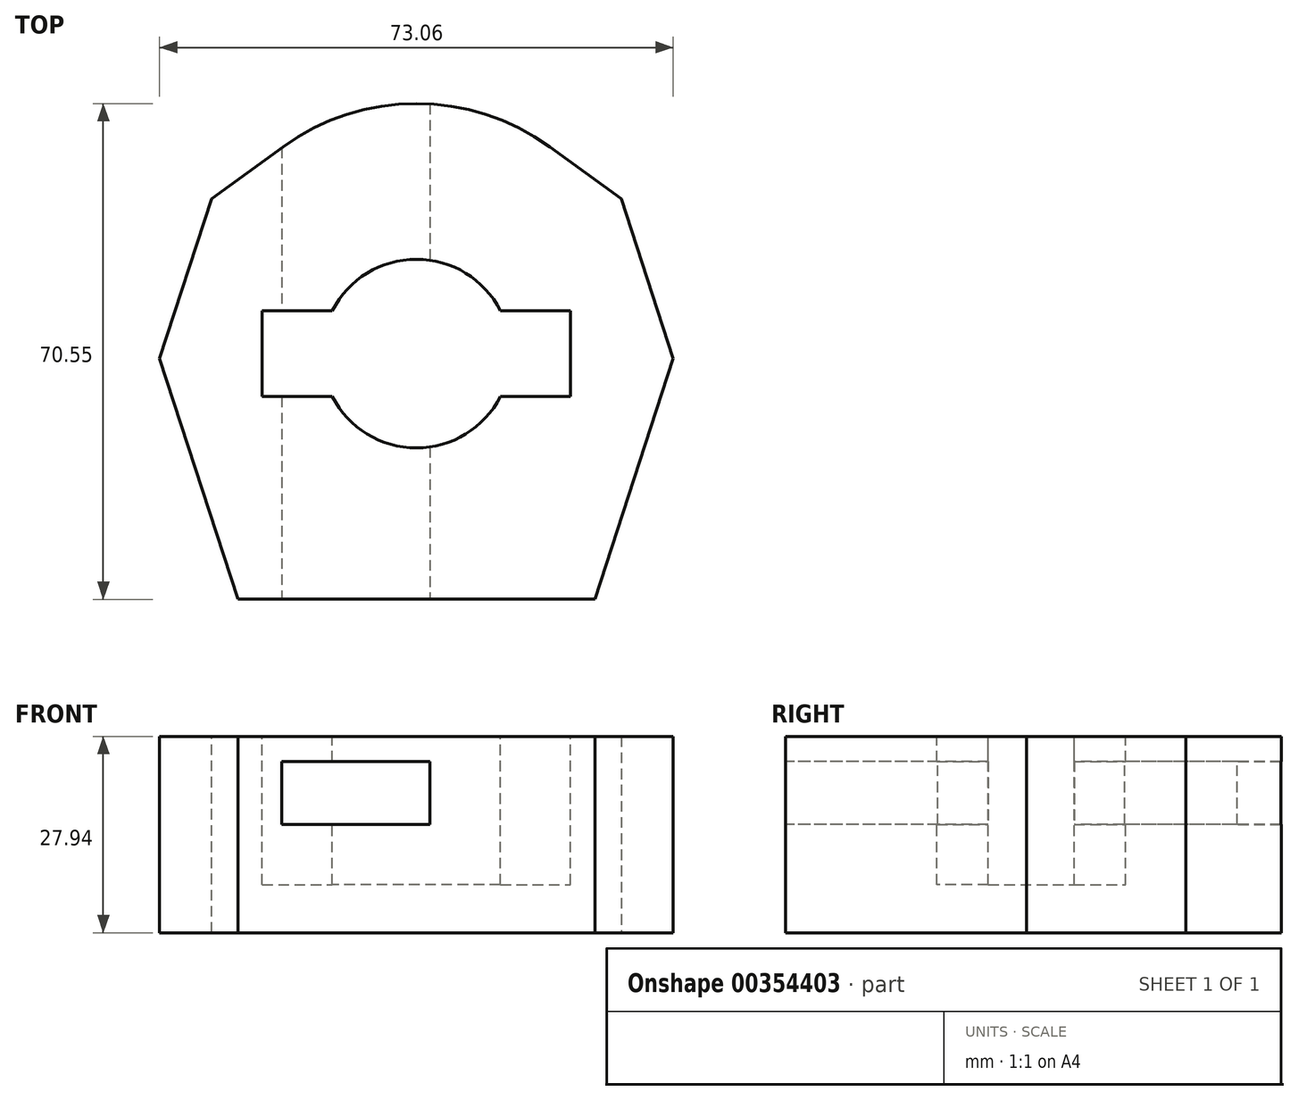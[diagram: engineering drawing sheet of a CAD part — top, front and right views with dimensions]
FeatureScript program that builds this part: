
annotation { "Feature Type Name" : "Feature", "Feature Type Description" : "" }
export const myFeature = defineFeature(function(context is Context, id is Id, definition is map)
    precondition{}
    {
        {
            var Q0;
            Q0=qCreatedBy(makeId("Top.planeOp"),FACE);
            var sketch = newSketch(context, id + "F0", { "sketchPlane" : qUnion([Q0])});
            skCircle(sketch, "E0.cCircle", {"center": v(0, 0) * mm, "radius": 34.96 * mm, "construction": true});
            skLineSegment(sketch, "E0.0", {"start": v(25.4, -34.96) * mm, "end": v(-25.4, -34.96) * mm});
            skLineSegment(sketch, "E0.1", {"start": v(-25.4, -34.96) * mm, "end": v(-41.1, 13.35) * mm});
            skLineSegment(sketch, "E0.2", {"start": v(-41.1, 13.35) * mm, "end": v(0, 43.2) * mm});
            skLineSegment(sketch, "E0.3", {"start": v(0, 43.2) * mm, "end": v(41.1, 13.35) * mm});
            skLineSegment(sketch, "E0.4", {"start": v(41.1, 13.35) * mm, "end": v(25.4, -34.96) * mm});
            skPoint(sketch, "E0.0.midPoint", {"position": v(0, -34.96) * mm});
            skSolve(sketch);
        }
        {
            var Q0;
            Q0 = qSketchRegion(id + "F0", true);
            extrude(context, id + "F1", {"entities" : qUnion([Q0]), "depth" : 27.94 * mm});
        }
        {
            var Q0;
            Q0=makeQuery(id+"F1.opExtrude","CAP_FACE",FACE,{"disambiguationData":[OSD([sQuery(id+"F0.wireOp",EDGE,"E0.0"),sQuery(id+"F0.wireOp",EDGE,"E0.1"),sQuery(id+"F0.wireOp",EDGE,"E0.2"),sQuery(id+"F0.wireOp",EDGE,"E0.3"),sQuery(id+"F0.wireOp",EDGE,"E0.4")])],"isStart":false});
            var sketch = newSketch(context, id + "F2", { "sketchPlane" : qUnion([Q0])});
            skCircle(sketch, "E1", {"center": v(0, 0) * mm, "radius": 13.43 * mm});
            skLineSegment(sketch, "E2.bottom", {"start": v(-21.93, -6.12) * mm, "end": v(21.93, -6.12) * mm});
            skLineSegment(sketch, "E2.top", {"start": v(-21.93, 6.12) * mm, "end": v(21.93, 6.12) * mm});
            skLineSegment(sketch, "E2.left", {"start": v(-21.93, -6.12) * mm, "end": v(-21.93, 6.12) * mm});
            skLineSegment(sketch, "E2.right", {"start": v(21.93, -6.12) * mm, "end": v(21.93, 6.12) * mm});
            skSolve(sketch);
        }
        {
            var Q0;
            Q0 = qSketchRegion(id + "F2", true);
            extrude(context, id + "F3", {"entities" : qUnion([Q0]), "operationType" : NewBodyOperationType.REMOVE, "oppositeDirection" : true, "depth" : 21.08 * mm});
        }
        {
            var Q0;
            Q0=makeQuery(id+"F1.opExtrude","SWEPT_EDGE",EDGE,{"disambiguationData":[OSD([sQuery(id+"F0.wireOp",EDGE,"E0.3"),sQuery(id+"F0.wireOp",EDGE,"E0.4")])]});
            var Q1;
            Q1=makeQuery(id+"F1.opExtrude","SWEPT_EDGE",EDGE,{"disambiguationData":[OSD([sQuery(id+"F0.wireOp",EDGE,"E0.1"),sQuery(id+"F0.wireOp",EDGE,"E0.2")])]});
            chamfer(context, id + "F4", {"entities" : qUnion([Q0, Q1]), "width" : 20.32 * mm, "tangentPropagation" : true});
        }
        {
            var Q0;
            Q0=makeQuery(id+"F1.opExtrude","SWEPT_EDGE",EDGE,{"disambiguationData":[OSD([sQuery(id+"F0.wireOp",EDGE,"E0.2"),sQuery(id+"F0.wireOp",EDGE,"E0.3")])]});
            fillet(context, id + "F5", {"entities" : qUnion([Q0]), "radius" : 32.28 * mm, "tangentPropagation" : true, "allowEdgeOverflow" : false});
        }
        {
            var Q0;
            Q0=makeQuery(id+"F1.opExtrude","SWEPT_FACE",FACE,{"disambiguationData":[OSD([sQuery(id+"F0.wireOp",EDGE,"E0.0")])]});
            var sketch = newSketch(context, id + "F6", { "sketchPlane" : qUnion([Q0])});
            skLineSegment(sketch, "E3.bottom", {"start": v(-19.17, 24.37) * mm, "end": v(1.9, 24.37) * mm});
            skLineSegment(sketch, "E3.top", {"start": v(-19.17, 15.4) * mm, "end": v(1.9, 15.4) * mm});
            skLineSegment(sketch, "E3.left", {"start": v(-19.17, 24.37) * mm, "end": v(-19.17, 15.4) * mm});
            skLineSegment(sketch, "E3.right", {"start": v(1.9, 24.37) * mm, "end": v(1.9, 15.4) * mm});
            skPoint(sketch, "E3.middle", {"position": v(-8.64, 19.89) * mm});
            skCircle(sketch, "E4.cCircle", {"center": v(-8.64, 19.89) * mm, "radius": 4.48 * mm, "construction": true});
            skLineSegment(sketch, "E4.0", {"start": v(-6.05, 15.4) * mm, "end": v(-11.23, 15.4) * mm});
            skLineSegment(sketch, "E4.1", {"start": v(-11.23, 15.4) * mm, "end": v(-13.82, 19.89) * mm});
            skLineSegment(sketch, "E4.2", {"start": v(-13.82, 19.89) * mm, "end": v(-11.23, 24.37) * mm});
            skLineSegment(sketch, "E4.3", {"start": v(-11.23, 24.37) * mm, "end": v(-6.05, 24.37) * mm});
            skLineSegment(sketch, "E4.4", {"start": v(-6.05, 24.37) * mm, "end": v(-3.46, 19.89) * mm});
            skLineSegment(sketch, "E4.5", {"start": v(-3.46, 19.89) * mm, "end": v(-6.05, 15.4) * mm});
            skPoint(sketch, "E4.0.midPoint", {"position": v(-8.64, 15.4) * mm});
            skSolve(sketch);
        }
        {
            var Q0;
            Q0 = qSketchRegion(id + "F6", true);
            extrude(context, id + "F7", {"entities" : qUnion([Q0]), "operationType" : NewBodyOperationType.REMOVE, "oppositeDirection" : true, "depth" : 79.76 * mm});
        }
    });
